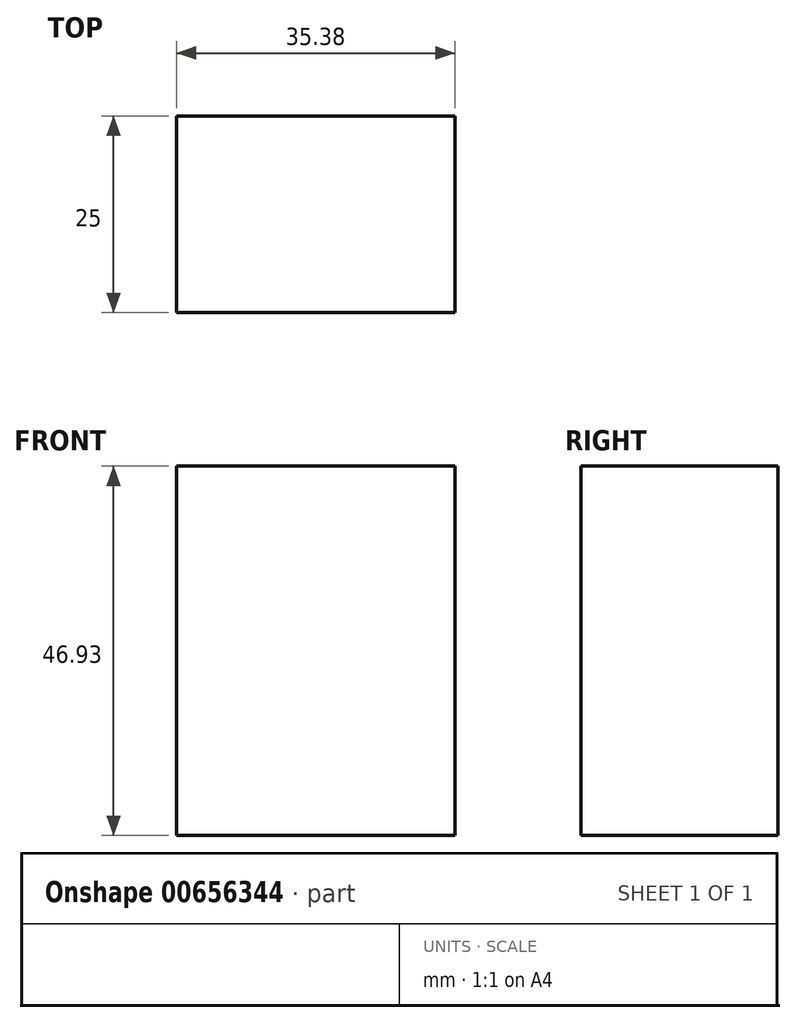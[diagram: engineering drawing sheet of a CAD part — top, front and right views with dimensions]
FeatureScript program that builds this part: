
annotation { "Feature Type Name" : "Feature", "Feature Type Description" : "" }
export const myFeature = defineFeature(function(context is Context, id is Id, definition is map)
    precondition{}
    {
        {
            var Q0;
            Q0=qCreatedBy(makeId("Front.planeOp"),FACE);
            var sketch = newSketch(context, id + "F0", { "sketchPlane" : qUnion([Q0])});
            skLineSegment(sketch, "E0.bottom", {"start": v(-82.61, 8.03) * mm, "end": v(-47.23, 8.03) * mm});
            skLineSegment(sketch, "E0.top", {"start": v(-82.61, 54.96) * mm, "end": v(-47.23, 54.96) * mm});
            skLineSegment(sketch, "E0.left", {"start": v(-82.61, 8.03) * mm, "end": v(-82.61, 54.96) * mm});
            skLineSegment(sketch, "E0.right", {"start": v(-47.23, 8.03) * mm, "end": v(-47.23, 54.96) * mm});
            skPoint(sketch, "E0.middle", {"position": v(-64.92, 31.5) * mm});
            skSolve(sketch);
        }
        {
            var Q0;
            Q0=makeQuery(id+"F0.imprint","IMPRINT",FACE,{"disambiguationData":[TD([[makeQuery(id+"F0.imprint","IMPRINT",EDGE,{"derivedFrom":sQuery(id+"F0.wireOp",EDGE,"E0.bottom")}),1.0]])]});
            extrude(context, id + "F1", {"entities" : qUnion([Q0]), "depth" : 25 * mm, "offsetDistance" : 25 * mm});
        }
    });
